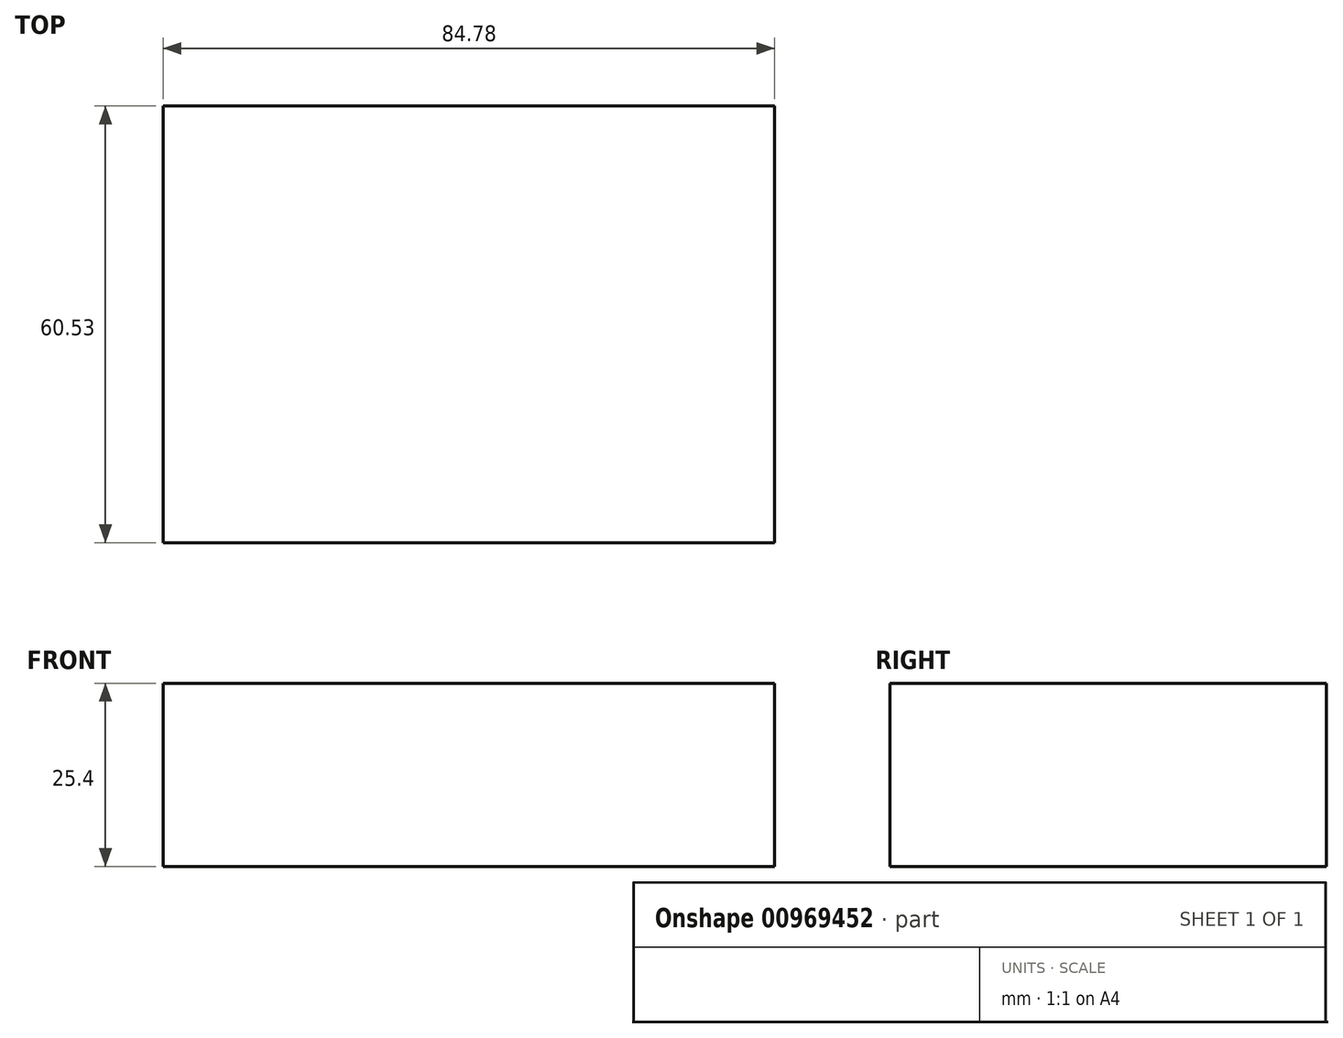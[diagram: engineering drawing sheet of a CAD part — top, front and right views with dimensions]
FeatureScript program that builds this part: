
annotation { "Feature Type Name" : "Feature", "Feature Type Description" : "" }
export const myFeature = defineFeature(function(context is Context, id is Id, definition is map)
    precondition{}
    {
        {
            var Q0;
            Q0=qCreatedBy(makeId("Top.planeOp"),FACE);
            var sketch = newSketch(context, id + "F0", { "sketchPlane" : qUnion([Q0])});
            skLineSegment(sketch, "E0.bottom", {"start": v(0, 0) * mm, "end": v(-84.78, 0) * mm});
            skLineSegment(sketch, "E0.top", {"start": v(0, 60.53) * mm, "end": v(-84.78, 60.53) * mm});
            skLineSegment(sketch, "E0.left", {"start": v(0, 0) * mm, "end": v(0, 60.53) * mm});
            skLineSegment(sketch, "E0.right", {"start": v(-84.78, 0) * mm, "end": v(-84.78, 60.53) * mm});
            skSolve(sketch);
        }
        {
            var Q0;
            Q0=makeQuery(id+"F0.imprint","IMPRINT",FACE,{"disambiguationData":[TD([[makeQuery(id+"F0.imprint","IMPRINT",EDGE,{"derivedFrom":sQuery(id+"F0.wireOp",EDGE,"E0.bottom")}),-1.0]])]});
            extrude(context, id + "F1", {"entities" : qUnion([Q0]), "depth" : 25.4 * mm, "offsetDistance" : 25.4 * mm});
        }
    });
